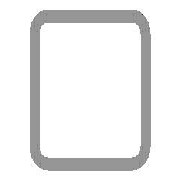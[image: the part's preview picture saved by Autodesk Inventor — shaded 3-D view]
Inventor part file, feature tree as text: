
AUTODESK INVENTOR PART (.ipt)
format: ipt  version: 2024.2 (Build 282272000, 272)  size: 129,536 bytes
history: native  units: mm (DEFAULTED — no unit token found)
features: other x4, sketch x1, plane x1
ambient origin geometry x8: Origin, YZ Plane, XZ Plane, XY Plane, X Axis, Y Axis, Z Axis, Center Point
bodies: Solid1 (feature_tree), Body (feature_tree)
feature tree (6):
  parser-record x1  (decoder bookkeeping rows leaked as tree rows — omitted from the tree; the rows remain in map.json)
  other  "Driven Length"
  other  "Start Plane"
  other  "End Plane"
  sketch  "Sketch3"  dims[d3=535.0mm d4=0.0mm d7=6.0mm d9=50.0mm d11=50.0mm d12=3.0mm d13=20.0mm d14=555.0mm d15=25.0mm d16=25.0mm d17=90.0deg d18=535.0mm]
  plane  "Work Plane3"
